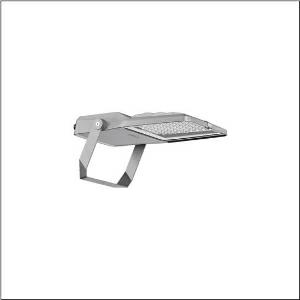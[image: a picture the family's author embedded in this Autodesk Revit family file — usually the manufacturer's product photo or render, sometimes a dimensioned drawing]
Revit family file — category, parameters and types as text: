
# Revit family: floodlight_fl_21_mini___pl61_5xa7775b2c1a_33c0
name_source: partatom
category: Lighting Fixtures
units: mm (PartAtom-declared; Revit-internal decimal feet)

## family parameters
Cut with Voids When Loaded = No
Host = Face
Light Source = No
Part Type = Normal
Room Calculation Point = No
Round Connector Dimension = Use Diameter
Shared = No

## types (1)
- --- (1 x LED, 6110 lm, 45.7 W, 3000K)
    Apparent Load = 46 VA
    CIE Flux Codes = 33 65 98 100 100
    Color Rendering = 70
    Color Temperature = 3000K
    Default Elevation = 1800 mm
    Description = Floodlight FL 21 mini, floodlight, primary light control with lens, of PMMA, primary optical cover: protective disc, of toughened safety glass, transparent, light distribution: PL61, light emission: direct distribution, installation type: surface-mounted, LED, High Power LED, rated luminous flux: 6.110lm, luminous efficacy: 134lm/W, light colour: 730, colour temperature: 3000K, control gear: Smart Interface (Zhaga), control: flexible luminous flux parameterisation, time-dependent luminous flux control, constant luminous flux control, overheat protection, pre-setting: logarithmic dimming characteristic, with terminal, 6-pole, mains connection: 220..240V, AC, 50/60Hz, start of lifetime: 46W, end of service life: 48W, reduction: 22W, luminaire housing, of diecast aluminium, powder-coated, Siteco® metallic grey (DB 702S), corrosivity category C5 mid according to DIN EN ISO 12944, suitable for swimming pools, chlorine-resistant, sealing non-destructively replaceable, mounting bracket, of steel, galvanised, powder-coated, Siteco® metallic grey (DB 702S), Smart Interface above, protection rating (complete): IP66, insulation class (complete): insulation class II (safety insulation), certification: CE, ENEC, VDE, protection symbol: D, impact resistance: IK08, permissible operating ambient temperature: -40..+40°C, permissible operating ambient temperature for outdoor applications: -40..+50°C, standard: DIN EN 12944, LABS conformity tested according to VDMA 24364:2018-05, packaging unit: 1 piece

Light Distribution: PL61
    Height = 70 mm
    Lamp = 1 x LED
    Lamp Light Flux = 6110 lm
    Lamp Power = 45.7 W
    Lamp count = 1
    Length = 485 mm
    Luminous efficacy = 134 lm/W
    Manufacturer = Siteco
    ModVariant = No
    Model = 5XA7775B2C1A
    Number of Poles = 1
    OnlyDefault = Yes
    Power Factor = 1
    Product Name = Floodlight FL 21 mini | PL61
    Product group = floodlight | pylon annexe
    ProductGroupID = 6201
    Protection Class = Protection class II
    Protection Degree = IP 66
    RLX_Detail_Level = 1
    RLX_Emergency_Light_Flux = 0 lm
    RLX_Emergency_Type = 0
    RLX_Emergency_Type_DB = No
    RlxData = <blob elided: 96021 chars, md5=b8c9a62b>
    Socket = socket
    Standby Power = 0 W
    System Light Flux = 6110 lm
    System Power = 46 W
    Type Comments = factory setting: luminous flux: 100 % | dim-lin: 254 | 463 mA
    Type Image = l_1006845.jpg
    URL = http://relux.com
    VarID = @adj_193701
    Voltage = 0 V
    Weight = 0.00 kg
    Width = 337 mm

## geometry (parser evidence)
native form markers: Blend x4, Sweep x12
no freeform markers — native parametric forms only
